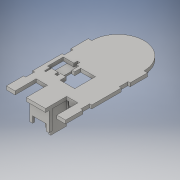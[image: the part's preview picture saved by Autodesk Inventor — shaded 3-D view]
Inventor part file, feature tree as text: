
AUTODESK INVENTOR PART (.ipt)
format: ipt  version: 2016 (Build 200138000, 138)  size: 493,056 bytes
history: native  units: in
note: dims shown in document units (in); Inventor stores cm internally (conversion verified against a paired STEP export)
features: reference x37, extrude x25, sketch x24, plane x6, projected_geometry x1
ambient origin geometry x8: Origin, YZ Plane, XZ Plane, XY Plane, X Axis, Y Axis, Z Axis, Center Point
bodies: Solid1 (feature_tree)
feature tree (93):
  extrude  "Extrusion1"  Depth=3.0in
  extrude  "Extrusion2"  Depth=0.0787in
  extrude  "Extrusion3"  Depth=1.0in
  extrude  "Extrusion5"  Depth=1.0in TaperAngle=0.0deg
  plane  "Work Plane1"
  extrude  "Extrusion6"  Depth=0.0787in
  extrude  "Extrusion9"  Depth=0.0787in
  extrude  "Extrusion14"  Depth=0.1575in
  extrude  "Extrusion15"  Depth=1.25in
  plane  "Work Plane2"
  extrude  "Extrusion16"  Depth=0.1575in
  extrude  "Extrusion17"  Depth=0.9201in TaperAngle=0.0deg
  extrude  "Extrusion18"  Depth=0.1969in
  plane  "Work Plane3"
  extrude  "Extrusion20"  Depth=0.1969in TaperAngle=0.0deg
  extrude  "Extrusion21"  Depth=0.1181in TaperAngle=0.0deg
  plane  "Work Plane4"
  plane  "Work Plane5"
  extrude  "Extrusion23"  Depth=0.1181in
  extrude  "Extrusion24"  Depth=0.1969in TaperAngle=0.0deg
  plane  "Work Plane6"
  extrude  "Extrusion25"  Depth=0.35in
  extrude  "Extrusion26"  Depth=0.2in
  extrude  "Extrusion27"  Depth=0.1969in TaperAngle=0.0deg
  extrude  "Extrusion28"  Depth=1.5in
  extrude  "Extrusion29"  Depth=0.7in
  extrude  "Extrusion30"  Depth=0.1181in TaperAngle=0.0deg
  extrude  "Extrusion31"  Depth=1.0in
  extrude  "Extrusion34"  Depth=0.5in
  sketch  "Sketch36"  dims[d105=0.1181in d106=0.5in]
  extrude  "Extrusion35"  Depth=0.5in
  extrude  "Extrusion36"  Depth=0.2in TaperAngle=0.0deg
  sketch  "Sketch1"  dims[d0=4.5in d1=3.0in]
  sketch  "Sketch2"  dims[d2=0.1969in d3=0.0in d5=0.0787in]
  reference  "Reference1"
  reference  "Reference2"
  sketch  "Sketch3"  dims[d6=1.0in d7=0.0in d8=1.0827in]
  sketch  "Sketch5"  dims[d9=0.3937in d10=1.0in d11=0.0in]
  reference  "Reference14"
  reference  "Reference15"
  reference  "Reference16"
  reference  "Reference17"
  reference  "Reference18"
  sketch  "Sketch6"  dims[d12=0.0787in d23=0.0098in]
  reference  "Reference19"
  sketch  "Sketch9"  dims[d24=0.1575in d25=0.0787in]
  projected_geometry  "Projected Loop2"
  sketch  "Sketch14"  dims[d26=0.0098in d27=0.1575in]
  sketch  "Sketch15"  dims[d28=0.1181in d29=0.0in d30=1.25in]
  sketch  "Sketch16"  dims[d31=0.1575in d32=0.1575in]
  reference  "Reference30"
  sketch  "Sketch17"  dims[d33=0.1181in d34=0.0in d46=0.9201in d47=0.0in]
  reference  "Reference31"
  reference  "Reference32"
  reference  "Reference33"
  reference  "Reference35"
  reference  "Reference36"
  reference  "Reference37"
  reference  "Reference38"
  reference  "Reference39"
  reference  "Reference40"
  reference  "Reference41"
  reference  "Reference42"
  reference  "Reference43"
  reference  "Reference44"
  reference  "Reference45"
  reference  "Reference46"
  reference  "Reference47"
  reference  "Reference48"
  reference  "Reference49"
  sketch  "Sketch20"  dims[d58=0.1969in d59=0.1969in]
  reference  "Reference50"
  sketch  "Sketch21"  dims[d60=0.1969in d61=0.1969in d62=0.0in]
  sketch  "Sketch23"  dims[d63=1.0in d64=0.0in d65=0.1181in d66=0.0in]
  reference  "Reference53"
  reference  "Reference54"
  sketch  "Sketch24"  dims[d67=0.1969in d68=0.0in d69=0.1181in]
  sketch  "Sketch25"  dims[d70=0.1181in d71=0.1969in d72=0.0in]
  reference  "Reference55"
  reference  "Reference56"
  sketch  "Sketch26"  dims[d75=0.0394in d76=0.35in]
  reference  "Reference57"
  reference  "Reference58"
  sketch  "Sketch28"  dims[d77=0.1628in d78=0.2in]
  sketch  "Sketch29"  dims[d79=0.0787in d80=0.0in d81=0.1969in d82=0.0in]
  sketch  "Sketch30"  dims[d89=1.5in d90=1.5in]
  reference  "Reference59"
  sketch  "Sketch31"  dims[d91=0.1181in d92=0.0in d93=0.7in]
  sketch  "Sketch32"  dims[d94=1.26in d95=0.0in d96=0.1181in d97=0.0in]
  sketch  "Sketch35"  dims[d98=0.1181in d99=0.0in d104=1.0in]
  reference  "Reference61"
  sketch  "Sketch37"  dims[d107=1.0in d108=0.5in d109=10.0in d110=0.0in d111=0.0197in d112=0.0197in d113=0.325in d114=0.197in d115=0.0in d116=0.1969in d117=0.1969in d118=0.1181in d119=0.1969in d120=0.0in d121=0.1575in d122=0.0in d123=0.1in d124=0.0in d132=1.0in d133=0.0in d134=0.5in d135=0.5in d136=0.0039in d137=0.0039in d138=0.0984in d139=0.0984in d140=0.0039in d141=0.0984in d142=1.61in d143=0.0in d144=0.2in d145=0.0in]
  reference  "Reference62"
